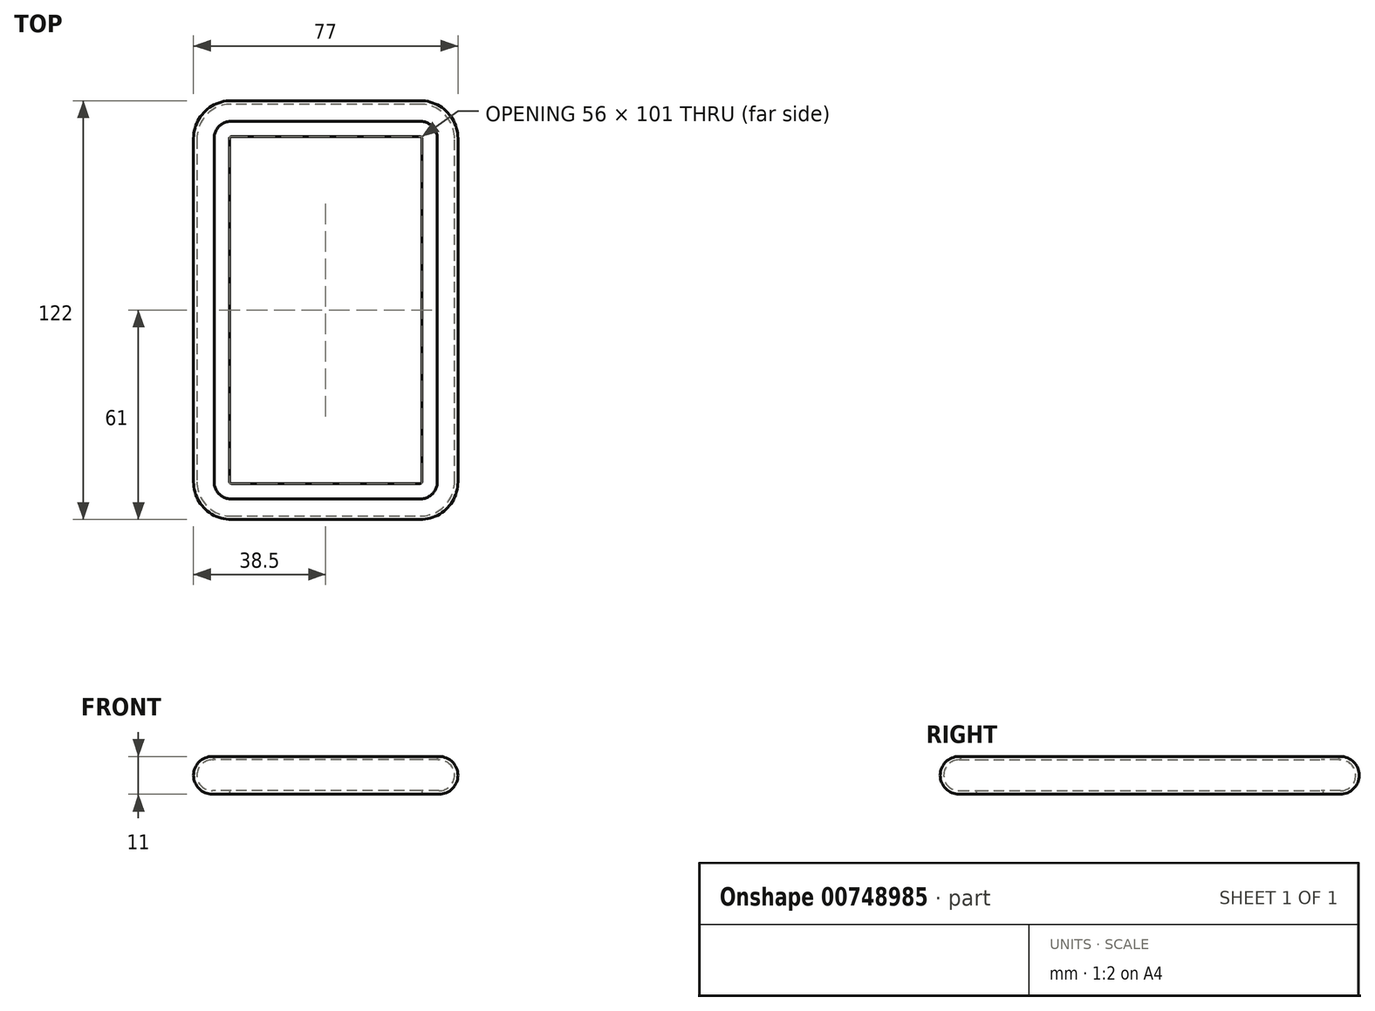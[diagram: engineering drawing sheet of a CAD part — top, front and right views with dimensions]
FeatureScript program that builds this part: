
annotation { "Feature Type Name" : "Feature", "Feature Type Description" : "" }
export const myFeature = defineFeature(function(context is Context, id is Id, definition is map)
    precondition{}
    {
        {
            var Q0;
            Q0=qCreatedBy(makeId("Top.planeOp"),FACE);
            var sketch = newSketch(context, id + "F0", { "sketchPlane" : qUnion([Q0])});
            skLineSegment(sketch, "E0.bottom", {"start": v(-27.5, 60) * mm, "end": v(27.5, 60) * mm});
            skLineSegment(sketch, "E0.top", {"start": v(-27.5, -60) * mm, "end": v(27.5, -60) * mm});
            skLineSegment(sketch, "E0.left", {"start": v(-37.5, 50) * mm, "end": v(-37.5, -50) * mm});
            skLineSegment(sketch, "E0.right", {"start": v(37.5, 50) * mm, "end": v(37.5, -50) * mm});
            skPoint(sketch, "E0.middle", {"position": v(0, 0) * mm});
            skPoint(sketch, "E1.visualSharp", {"position": v(-37.5, 60) * mm});
            skArc(sketch, "E1.filletArc", {"start": v(-27.5, 60) * mm, "mid": v(-34.57, 57.07) * mm, "end": v(-37.5, 50) * mm});
            skPoint(sketch, "E2.visualSharp", {"position": v(37.5, 60) * mm});
            skArc(sketch, "E2.filletArc", {"start": v(37.5, 50) * mm, "mid": v(34.57, 57.07) * mm, "end": v(27.5, 60) * mm});
            skPoint(sketch, "E3.visualSharp", {"position": v(37.5, -60) * mm});
            skArc(sketch, "E3.filletArc", {"start": v(27.5, -60) * mm, "mid": v(34.57, -57.07) * mm, "end": v(37.5, -50) * mm});
            skPoint(sketch, "E4.visualSharp", {"position": v(-37.5, -60) * mm});
            skArc(sketch, "E4.filletArc", {"start": v(-37.5, -50) * mm, "mid": v(-34.57, -57.07) * mm, "end": v(-27.5, -60) * mm});
            skSolve(sketch);
        }
        {
            var Q0;
            Q0=qCreatedBy(makeId("Front.planeOp"),FACE);
            var sketch = newSketch(context, id + "F1", { "sketchPlane" : qUnion([Q0])});
            skLineSegment(sketch, "E5", {"start": v(-37.5, 0) * mm, "end": v(37.5, 0) * mm, "construction": true});
            skArc(sketch, "E6", {"start": v(-33, 4.5) * mm, "mid": v(-37.5, 0) * mm, "end": v(-33, -4.5) * mm});
            skLineSegment(sketch, "E7", {"start": v(-33, -4.5) * mm, "end": v(-28, -4.5) * mm});
            skLineSegment(sketch, "E8", {"start": v(-28, -4.5) * mm, "end": v(-28, -5.5) * mm});
            skLineSegment(sketch, "E9", {"start": v(-28, -5.5) * mm, "end": v(-33, -5.5) * mm});
            skArc(sketch, "E10", {"start": v(-33, -5.5) * mm, "mid": v(-38.5, 0) * mm, "end": v(-33, 5.5) * mm});
            skArc(sketch, "E11", {"start": v(-33, 5.5) * mm, "mid": v(-32.5, 5) * mm, "end": v(-33, 4.5) * mm});
            skSolve(sketch);
        }
        {
            var Q0;
            Q0 = qSketchRegion(id + "F1", true);
            var Q1;
            Q1 = qConstructionFilter(qBodyType(qCreatedBy(id + "F0" ,EDGE), BodyType.WIRE), ConstructionObject.NO);
            sweep(context, id + "F2", {"profiles" : qUnion([Q0]), "path" : qUnion([Q1])});
        }
    });
